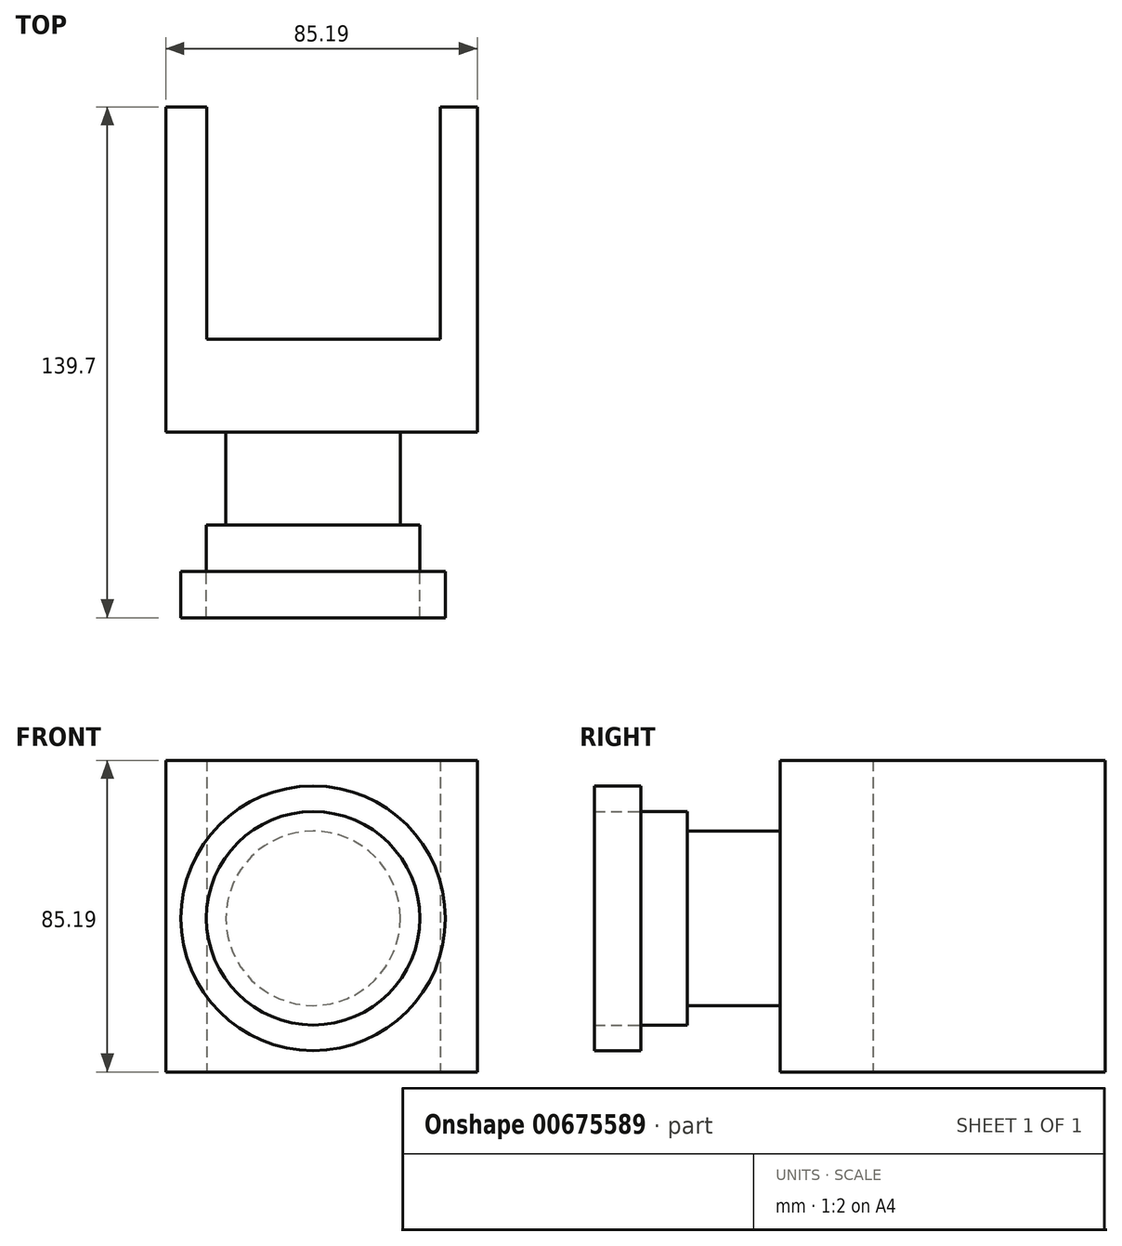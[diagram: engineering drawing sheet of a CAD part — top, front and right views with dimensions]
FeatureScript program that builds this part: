
annotation { "Feature Type Name" : "Feature", "Feature Type Description" : "" }
export const myFeature = defineFeature(function(context is Context, id is Id, definition is map)
    precondition{}
    {
        {
            var Q0;
            Q0=qCreatedBy(makeId("Front.planeOp"),FACE);
            var sketch = newSketch(context, id + "F0", { "sketchPlane" : qUnion([Q0])});
            skLineSegment(sketch, "E0.bottom", {"start": v(-38.13, 37.27) * mm, "end": v(47.06, 37.27) * mm});
            skLineSegment(sketch, "E0.top", {"start": v(-38.13, -47.92) * mm, "end": v(47.06, -47.92) * mm});
            skLineSegment(sketch, "E0.left", {"start": v(-38.13, 37.27) * mm, "end": v(-38.13, -47.92) * mm});
            skLineSegment(sketch, "E0.right", {"start": v(47.06, 37.27) * mm, "end": v(47.06, -47.92) * mm});
            skSolve(sketch);
        }
        {
            var Q0;
            Q0 = qSketchRegion(id + "F0", true);
            extrude(context, id + "F1", {"entities" : qUnion([Q0]), "depth" : 25.4 * mm, "offsetDistance" : 25.4 * mm});
        }
        {
            var Q0;
            Q0=makeQuery(id+"F1.opExtrude","CAP_FACE",FACE,{"disambiguationData":[OSD([sQuery(id+"F0.wireOp",EDGE,"E0.bottom"),sQuery(id+"F0.wireOp",EDGE,"E0.top"),sQuery(id+"F0.wireOp",EDGE,"E0.left"),sQuery(id+"F0.wireOp",EDGE,"E0.right")])],"isStart":true});
            var sketch = newSketch(context, id + "F2", { "sketchPlane" : qUnion([Q0])});
            skLineSegment(sketch, "E1.bottom", {"start": v(-47.06, 37.27) * mm, "end": v(-36.98, 37.27) * mm});
            skLineSegment(sketch, "E1.top", {"start": v(-47.06, -47.92) * mm, "end": v(-36.98, -47.92) * mm});
            skLineSegment(sketch, "E1.left", {"start": v(-47.06, 37.27) * mm, "end": v(-47.06, -47.92) * mm});
            skLineSegment(sketch, "E1.right", {"start": v(-36.98, 37.27) * mm, "end": v(-36.98, -47.92) * mm});
            skLineSegment(sketch, "E2.bottom", {"start": v(38.13, 37.27) * mm, "end": v(26.9, 37.27) * mm});
            skLineSegment(sketch, "E2.top", {"start": v(38.13, -47.92) * mm, "end": v(26.9, -47.92) * mm});
            skLineSegment(sketch, "E2.left", {"start": v(38.13, 37.27) * mm, "end": v(38.13, -47.92) * mm});
            skLineSegment(sketch, "E2.right", {"start": v(26.9, 37.27) * mm, "end": v(26.9, -47.92) * mm});
            skSolve(sketch);
        }
        {
            var Q0;
            Q0 = qSketchRegion(id + "F2", true);
            extrude(context, id + "F3", {"entities" : qUnion([Q0]), "operationType" : NewBodyOperationType.ADD, "depth" : 63.5 * mm, "offsetDistance" : 25.4 * mm});
        }
        {
            var Q0;
            Q0=makeQuery(id+"F1.opExtrude","CAP_FACE",FACE,{"disambiguationData":[OSD([sQuery(id+"F0.wireOp",EDGE,"E0.bottom"),sQuery(id+"F0.wireOp",EDGE,"E0.top"),sQuery(id+"F0.wireOp",EDGE,"E0.left"),sQuery(id+"F0.wireOp",EDGE,"E0.right")])],"isStart":false});
            var sketch = newSketch(context, id + "F4", { "sketchPlane" : qUnion([Q0])});
            skCircle(sketch, "E3", {"center": v(2.16, -5.9) * mm, "radius": 23.85 * mm});
            skSolve(sketch);
        }
        {
            var Q0;
            Q0 = qSketchRegion(id + "F4", true);
            extrude(context, id + "F5", {"entities" : qUnion([Q0]), "operationType" : NewBodyOperationType.ADD, "depth" : 25.4 * mm, "offsetDistance" : 25.4 * mm});
        }
        {
            var Q0;
            Q0=makeQuery(id+"F5.opExtrude","CAP_FACE",FACE,{"disambiguationData":[OSD([sQuery(id+"F4.wireOp",EDGE,"E3")])],"isStart":false});
            var sketch = newSketch(context, id + "F6", { "sketchPlane" : qUnion([Q0])});
            skCircle(sketch, "E4", {"center": v(2.16, -5.9) * mm, "radius": 29.18 * mm});
            skSolve(sketch);
        }
        {
            var Q0;
            Q0 = qSketchRegion(id + "F6", true);
            extrude(context, id + "F7", {"entities" : qUnion([Q0]), "operationType" : NewBodyOperationType.ADD, "depth" : 12.7 * mm, "offsetDistance" : 25.4 * mm});
        }
        {
            var Q0;
            Q0=makeQuery(id+"F7.opExtrude","CAP_FACE",FACE,{"disambiguationData":[OSD([sQuery(id+"F6.wireOp",EDGE,"E4")])],"isStart":false});
            var sketch = newSketch(context, id + "F8", { "sketchPlane" : qUnion([Q0])});
            skCircle(sketch, "E5", {"center": v(2.16, -5.9) * mm, "radius": 36.18 * mm});
            skSolve(sketch);
        }
        {
            var Q0;
            Q0=makeQuery(id+"F8.imprint","IMPRINT",FACE,{"disambiguationData":[TD([[makeQuery(id+"F8.imprint","IMPRINT",EDGE,{"derivedFrom":sQuery(id+"F8.wireOp",EDGE,"E5")}),1.0]])]});
            extrude(context, id + "F9", {"entities" : qUnion([Q0]), "depth" : 12.7 * mm, "offsetDistance" : 25.4 * mm});
        }
    });
